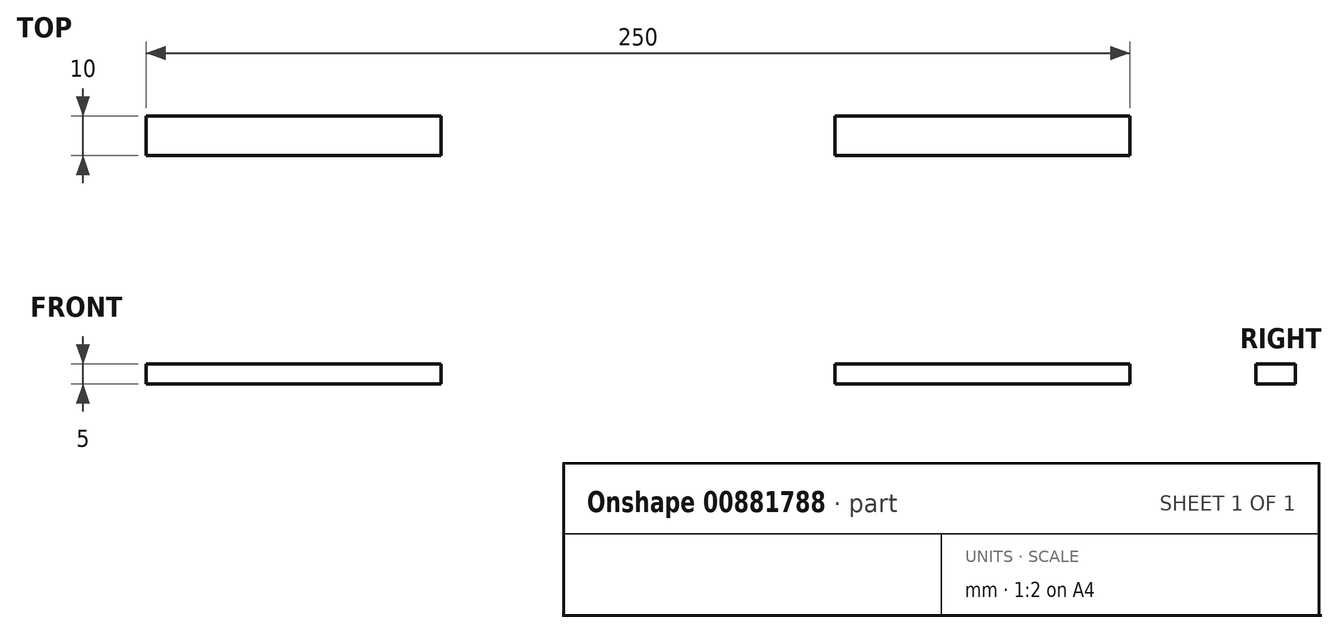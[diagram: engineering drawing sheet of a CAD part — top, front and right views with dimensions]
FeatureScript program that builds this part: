
annotation { "Feature Type Name" : "Feature", "Feature Type Description" : "" }
export const myFeature = defineFeature(function(context is Context, id is Id, definition is map)
    precondition{}
    {
        {
            var Q0;
            Q0=qCreatedBy(makeId("Top.planeOp"),FACE);
            var sketch = newSketch(context, id + "F0", { "sketchPlane" : qUnion([Q0])});
            skLineSegment(sketch, "E0.bottom", {"start": v(125, -32.5) * mm, "end": v(-125, -32.5) * mm});
            skLineSegment(sketch, "E0.top", {"start": v(125, 32.5) * mm, "end": v(-125, 32.5) * mm});
            skLineSegment(sketch, "E0.left", {"start": v(125, -32.5) * mm, "end": v(125, 32.5) * mm});
            skLineSegment(sketch, "E0.right", {"start": v(-125, -32.5) * mm, "end": v(-125, 32.5) * mm});
            skPoint(sketch, "E0.middle", {"position": v(0, 0) * mm});
            skLineSegment(sketch, "E1", {"start": v(0, 32.5) * mm, "end": v(0, 27.14) * mm, "construction": true});
            skLineSegment(sketch, "E2", {"start": v(-125, 0) * mm, "end": v(-114.37, 0) * mm, "construction": true});
            skLineSegment(sketch, "E3", {"start": v(-50, 32.5) * mm, "end": v(-50, 22.5) * mm});
            skLineSegment(sketch, "E4", {"start": v(-50, 22.5) * mm, "end": v(-125, 22.5) * mm});
            skLineSegment(sketch, "E5", {"start": v(-50, 32.5) * mm, "end": v(-125, 32.5) * mm});
            skLineSegment(sketch, "E6.MirrorCS", {"start": v(50, 32.5) * mm, "end": v(50, 22.5) * mm});
            skLineSegment(sketch, "E7.MirrorCS", {"start": v(50, 22.5) * mm, "end": v(125, 22.5) * mm});
            skLineSegment(sketch, "E8", {"start": v(-125, 22.5) * mm, "end": v(-125, 32.5) * mm});
            skLineSegment(sketch, "E9.MirrorCS", {"start": v(125, 22.5) * mm, "end": v(125, 32.5) * mm});
            skLineSegment(sketch, "E10.MirrorCS", {"start": v(50, 32.5) * mm, "end": v(125, 32.5) * mm});
            skLineSegment(sketch, "E11.MirrorCS", {"start": v(-50, -22.5) * mm, "end": v(-125, -22.5) * mm});
            skLineSegment(sketch, "E12.MirrorCS", {"start": v(-50, -32.5) * mm, "end": v(-50, -22.5) * mm});
            skLineSegment(sketch, "E13.MirrorCS", {"start": v(-50, -32.5) * mm, "end": v(-125, -32.5) * mm});
            skLineSegment(sketch, "E14.MirrorCS", {"start": v(-125, -22.5) * mm, "end": v(-125, -32.5) * mm});
            skLineSegment(sketch, "E15.MirrorCS", {"start": v(50, -22.5) * mm, "end": v(125, -22.5) * mm});
            skLineSegment(sketch, "E16.MirrorCS", {"start": v(50, -32.5) * mm, "end": v(50, -22.5) * mm});
            skLineSegment(sketch, "E17.MirrorCS", {"start": v(50, -32.5) * mm, "end": v(125, -32.5) * mm});
            skLineSegment(sketch, "E18.MirrorCS", {"start": v(125, 32.5) * mm, "end": v(125, -32.5) * mm});
            skSolve(sketch);
        }
        {
            var Q0;
            Q0=makeQuery(id+"F0.imprint","IMPRINT",FACE,{"disambiguationData":[TD([[makeQuery(id+"F0.imprint","IMPRINT",EDGE,{"derivedFrom":sQuery(id+"F0.wireOp",EDGE,"E0.bottom")}),-1.0]])]});
            extrude(context, id + "F1", {"entities" : qUnion([Q0]), "depth" : 5 * mm, "offsetDistance" : 25 * mm});
        }
    });
